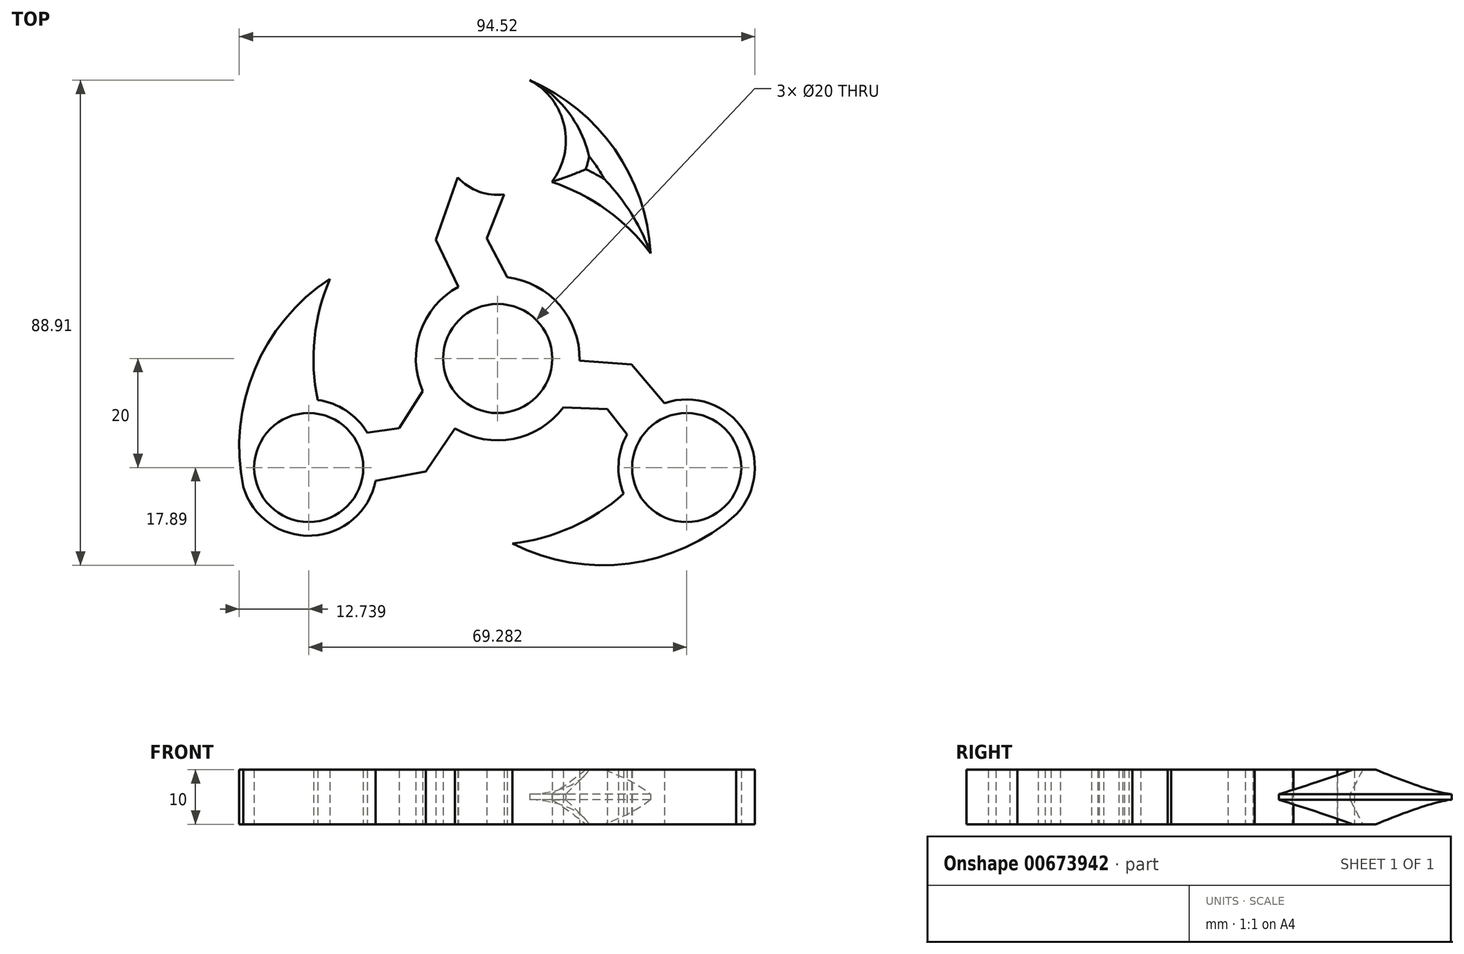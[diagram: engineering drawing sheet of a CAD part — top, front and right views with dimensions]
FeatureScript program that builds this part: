
annotation { "Feature Type Name" : "Feature", "Feature Type Description" : "" }
export const myFeature = defineFeature(function(context is Context, id is Id, definition is map)
    precondition{}
    {
        {
            var Q0;
            Q0=qCreatedBy(makeId("Top.planeOp"),FACE);
            var sketch = newSketch(context, id + "F0", { "sketchPlane" : qUnion([Q0])});
            skArc(sketch, "E0", {"start": v(-9.92, 38.75) * mm, "mid": v(0, -40) * mm, "end": v(9.92, 38.75) * mm});
            skCircle(sketch, "E1", {"center": v(0, 0) * mm, "radius": 10 * mm});
            skLineSegment(sketch, "E2", {"start": v(-5, 8.66) * mm, "end": v(-11.35, 21.78) * mm});
            skLineSegment(sketch, "E3", {"start": v(-11.35, 21.78) * mm, "end": v(-7.3, 33.18) * mm});
            skLineSegment(sketch, "E4", {"start": v(5, 8.66) * mm, "end": v(-2.01, 22.03) * mm});
            skLineSegment(sketch, "E5", {"start": v(-2.01, 22.03) * mm, "end": v(1.18, 30.07) * mm});
            skCircle(sketch, "E6", {"center": v(0, 40) * mm, "radius": 10 * mm});
            skCircle(sketch, "E7", {"center": v(0, 40) * mm, "radius": 12.5 * mm});
            skPoint(sketch, "E8.orphan", {"position": v(-5, 39.69) * mm});
            skPoint(sketch, "E9.orphan", {"position": v(5, 39.69) * mm});
            skCircle(sketch, "E10.1.0", {"center": v(-34.64, -20) * mm, "radius": 12.5 * mm});
            skCircle(sketch, "E10.1.1", {"center": v(-34.64, -20) * mm, "radius": 10 * mm});
            skLineSegment(sketch, "E10.1.2", {"start": v(-13.19, -20.72) * mm, "end": v(-25.08, -22.92) * mm});
            skLineSegment(sketch, "E10.1.3", {"start": v(-18.07, -12.76) * mm, "end": v(-26.63, -14.01) * mm});
            skLineSegment(sketch, "E10.1.4", {"start": v(-5, -8.66) * mm, "end": v(-13.19, -20.72) * mm});
            skLineSegment(sketch, "E10.1.5", {"start": v(-10, 0) * mm, "end": v(-18.07, -12.76) * mm});
            skCircle(sketch, "E10.2.0", {"center": v(34.64, -20) * mm, "radius": 12.5 * mm});
            skCircle(sketch, "E10.2.1", {"center": v(34.64, -20) * mm, "radius": 10 * mm});
            skLineSegment(sketch, "E10.2.2", {"start": v(24.54, -1.06) * mm, "end": v(32.39, -10.26) * mm});
            skLineSegment(sketch, "E10.2.3", {"start": v(20.08, -9.27) * mm, "end": v(25.45, -16.06) * mm});
            skLineSegment(sketch, "E10.2.4", {"start": v(10, 0) * mm, "end": v(24.54, -1.06) * mm});
            skLineSegment(sketch, "E10.2.5", {"start": v(5, -8.66) * mm, "end": v(20.08, -9.27) * mm});
            skCircle(sketch, "E11", {"center": v(0, 0) * mm, "radius": 15 * mm});
            skArc(sketch, "E12", {"start": v(28.04, 19.33) * mm, "mid": v(20.53, 39.6) * mm, "end": v(2.93, 52.15) * mm});
            skArc(sketch, "E13", {"start": v(28.04, 19.33) * mm, "mid": v(19.97, 27.24) * mm, "end": v(9.92, 32.4) * mm});
            skArc(sketch, "E14.1.0", {"start": v(-30.76, 14.62) * mm, "mid": v(-44.57, -2.02) * mm, "end": v(-46.63, -23.54) * mm});
            skArc(sketch, "E14.1.1", {"start": v(-30.76, 14.62) * mm, "mid": v(-33.58, 3.68) * mm, "end": v(-33.02, -7.6) * mm});
            skArc(sketch, "E14.2.0", {"start": v(2.72, -33.94) * mm, "mid": v(24.03, -37.59) * mm, "end": v(43.7, -28.61) * mm});
            skArc(sketch, "E14.2.1", {"start": v(2.72, -33.94) * mm, "mid": v(13.6, -30.92) * mm, "end": v(23.1, -24.8) * mm});
            skSolve(sketch);
        }
        {
            var Q0;
            {var subQ0=sQuery(id+"F0.wireOp",EDGE,"E6");var subQ1=sQuery(id+"F0.wireOp",EDGE,"E0");var subQ2=makeQuery(id+"F0.imprint","INTERSECT",VERTEX,{"disambiguationData":[OD(1.0)],"derivedFrom":[subQ1,subQ0]});Q0=makeQuery(id+"F0.imprint","IMPRINT",FACE,{"disambiguationData":[TD([[makeQuery(id+"F0.imprint","IMPRINT",EDGE,{"disambiguationData":[TD([[subQ2,1.0]])],"derivedFrom":subQ1}),1.0]])]});}
            var Q1;
            {var subQ0=sQuery(id+"F0.wireOp",EDGE,"E6");var subQ1=sQuery(id+"F0.wireOp",EDGE,"E0");var subQ2=makeQuery(id+"F0.imprint","INTERSECT",VERTEX,{"disambiguationData":[OD(0.0)],"derivedFrom":[subQ1,subQ0]});Q1=makeQuery(id+"F0.imprint","IMPRINT",FACE,{"disambiguationData":[TD([[makeQuery(id+"F0.imprint","IMPRINT",EDGE,{"disambiguationData":[TD([[subQ2,-1.0]])],"derivedFrom":subQ1}),-1.0]])]});}
            var Q2;
            {var subQ0=sQuery(id+"F0.wireOp",EDGE,"E6");var subQ1=sQuery(id+"F0.wireOp",EDGE,"E0");var subQ2=makeQuery(id+"F0.imprint","INTERSECT",VERTEX,{"disambiguationData":[OD(0.0)],"derivedFrom":[subQ1,subQ0]});Q2=makeQuery(id+"F0.imprint","IMPRINT",FACE,{"disambiguationData":[TD([[makeQuery(id+"F0.imprint","IMPRINT",EDGE,{"disambiguationData":[TD([[subQ2,-1.0]])],"derivedFrom":subQ1}),1.0]])]});}
            var Q3;
            {var subQ0=sQuery(id+"F0.wireOp",EDGE,"E6");var subQ1=sQuery(id+"F0.wireOp",EDGE,"E3");var subQ2=makeQuery(id+"F0.imprint","INTERSECT",VERTEX,{"derivedFrom":[subQ1,subQ0]});Q3=makeQuery(id+"F0.imprint","IMPRINT",FACE,{"disambiguationData":[TD([[makeQuery(id+"F0.imprint","IMPRINT",EDGE,{"disambiguationData":[TD([[subQ2,1.0]])],"derivedFrom":subQ1}),-1.0]])]});}
            var Q4;
            {var subQ5=sQuery(id+"F0.wireOp",EDGE,"E3");var subQ6=sQuery(id+"F0.wireOp",EDGE,"E2");var subQ7=makeQuery(id+"F0.imprint","INTERSECT",VERTEX,{"derivedFrom":[subQ6,subQ5]});Q4=makeQuery(id+"F0.imprint","IMPRINT",FACE,{"disambiguationData":[TD([[makeQuery(id+"F0.imprint","IMPRINT",EDGE,{"disambiguationData":[TD([[subQ7,1.0]])],"derivedFrom":subQ6}),-1.0]])]});}
            var Q5;
            {var subQ0=sQuery(id+"F0.wireOp",EDGE,"E2");var subQ1=sQuery(id+"F0.wireOp",EDGE,"E1");var subQ2=makeQuery(id+"F0.imprint","INTERSECT",VERTEX,{"derivedFrom":[subQ1,subQ0]});Q5=makeQuery(id+"F0.imprint","IMPRINT",FACE,{"disambiguationData":[TD([[makeQuery(id+"F0.imprint","IMPRINT",EDGE,{"disambiguationData":[TD([[subQ2,1.0]])],"derivedFrom":subQ1}),-1.0]])]});}
            var Q6;
            {var subQ0=sQuery(id+"F0.wireOp",EDGE,"E2");var subQ1=sQuery(id+"F0.wireOp",EDGE,"E1");var subQ2=makeQuery(id+"F0.imprint","INTERSECT",VERTEX,{"derivedFrom":[subQ1,subQ0]});Q6=makeQuery(id+"F0.imprint","IMPRINT",FACE,{"disambiguationData":[TD([[makeQuery(id+"F0.imprint","IMPRINT",EDGE,{"disambiguationData":[TD([[subQ2,-1.0]])],"derivedFrom":subQ1}),-1.0]])]});}
            var Q7;
            {var subQ0=sQuery(id+"F0.wireOp",EDGE,"E4");var subQ1=sQuery(id+"F0.wireOp",EDGE,"E1");var subQ2=makeQuery(id+"F0.imprint","INTERSECT",VERTEX,{"derivedFrom":[subQ1,subQ0]});Q7=makeQuery(id+"F0.imprint","IMPRINT",FACE,{"disambiguationData":[TD([[makeQuery(id+"F0.imprint","IMPRINT",EDGE,{"disambiguationData":[TD([[subQ2,1.0]])],"derivedFrom":subQ1}),-1.0]])]});}
            var Q8;
            {var subQ0=sQuery(id+"F0.wireOp",EDGE,"E10.2.4");var subQ1=sQuery(id+"F0.wireOp",EDGE,"E1");var subQ2=makeQuery(id+"F0.imprint","INTERSECT",VERTEX,{"derivedFrom":[subQ1,subQ0]});Q8=makeQuery(id+"F0.imprint","IMPRINT",FACE,{"disambiguationData":[TD([[makeQuery(id+"F0.imprint","IMPRINT",EDGE,{"disambiguationData":[TD([[subQ2,1.0]])],"derivedFrom":subQ1}),-1.0]])]});}
            var Q9;
            {var subQ0=sQuery(id+"F0.wireOp",EDGE,"E10.1.4");var subQ1=sQuery(id+"F0.wireOp",EDGE,"E1");var subQ2=makeQuery(id+"F0.imprint","INTERSECT",VERTEX,{"derivedFrom":[subQ1,subQ0]});Q9=makeQuery(id+"F0.imprint","IMPRINT",FACE,{"disambiguationData":[TD([[makeQuery(id+"F0.imprint","IMPRINT",EDGE,{"disambiguationData":[TD([[subQ2,-1.0]])],"derivedFrom":subQ1}),-1.0]])]});}
            var Q10;
            {var subQ0=sQuery(id+"F0.wireOp",EDGE,"E10.1.4");var subQ1=sQuery(id+"F0.wireOp",EDGE,"E1");var subQ2=makeQuery(id+"F0.imprint","INTERSECT",VERTEX,{"derivedFrom":[subQ1,subQ0]});Q10=makeQuery(id+"F0.imprint","IMPRINT",FACE,{"disambiguationData":[TD([[makeQuery(id+"F0.imprint","IMPRINT",EDGE,{"disambiguationData":[TD([[subQ2,1.0]])],"derivedFrom":subQ1}),-1.0]])]});}
            var Q11;
            {var subQ3=sQuery(id+"F0.wireOp",EDGE,"E10.1.0");var subQ6=sQuery(id+"F0.wireOp",EDGE,"E10.1.2");var subQ10=makeQuery(id+"F0.imprint","INTERSECT",VERTEX,{"derivedFrom":[subQ3,subQ6]});Q11=makeQuery(id+"F0.imprint","IMPRINT",FACE,{"disambiguationData":[TD([[makeQuery(id+"F0.imprint","IMPRINT",EDGE,{"disambiguationData":[TD([[subQ10,-1.0]])],"derivedFrom":subQ3}),-1.0]])]});}
            var Q12;
            {var subQ0=sQuery(id+"F0.wireOp",EDGE,"E10.1.2");var subQ1=sQuery(id+"F0.wireOp",EDGE,"E10.1.0");var subQ2=makeQuery(id+"F0.imprint","INTERSECT",VERTEX,{"derivedFrom":[subQ1,subQ0]});Q12=makeQuery(id+"F0.imprint","IMPRINT",FACE,{"disambiguationData":[TD([[makeQuery(id+"F0.imprint","IMPRINT",EDGE,{"disambiguationData":[TD([[subQ2,-1.0]])],"derivedFrom":subQ1}),1.0]])]});}
            var Q13;
            {var subQ0=sQuery(id+"F0.wireOp",EDGE,"E10.1.0");var subQ1=sQuery(id+"F0.wireOp",EDGE,"E0");var subQ2=makeQuery(id+"F0.imprint","INTERSECT",VERTEX,{"disambiguationData":[OD(0.0)],"derivedFrom":[subQ1,subQ0]});Q13=makeQuery(id+"F0.imprint","IMPRINT",FACE,{"disambiguationData":[TD([[makeQuery(id+"F0.imprint","IMPRINT",EDGE,{"disambiguationData":[TD([[subQ2,-1.0]])],"derivedFrom":subQ1}),-1.0]])]});}
            var Q14;
            {var subQ0=sQuery(id+"F0.wireOp",EDGE,"E10.1.0");var subQ1=sQuery(id+"F0.wireOp",EDGE,"E0");var subQ2=makeQuery(id+"F0.imprint","INTERSECT",VERTEX,{"disambiguationData":[OD(1.0)],"derivedFrom":[subQ1,subQ0]});Q14=makeQuery(id+"F0.imprint","IMPRINT",FACE,{"disambiguationData":[TD([[makeQuery(id+"F0.imprint","IMPRINT",EDGE,{"disambiguationData":[TD([[subQ2,1.0]])],"derivedFrom":subQ1}),1.0]])]});}
            var Q15;
            {var subQ3=sQuery(id+"F0.wireOp",EDGE,"E10.2.0");var subQ6=sQuery(id+"F0.wireOp",EDGE,"E10.2.2");var subQ10=makeQuery(id+"F0.imprint","INTERSECT",VERTEX,{"derivedFrom":[subQ3,subQ6]});Q15=makeQuery(id+"F0.imprint","IMPRINT",FACE,{"disambiguationData":[TD([[makeQuery(id+"F0.imprint","IMPRINT",EDGE,{"disambiguationData":[TD([[subQ10,-1.0]])],"derivedFrom":subQ3}),-1.0]])]});}
            var Q16;
            {var subQ0=sQuery(id+"F0.wireOp",EDGE,"E10.2.2");var subQ1=sQuery(id+"F0.wireOp",EDGE,"E10.2.0");var subQ2=makeQuery(id+"F0.imprint","INTERSECT",VERTEX,{"derivedFrom":[subQ1,subQ0]});Q16=makeQuery(id+"F0.imprint","IMPRINT",FACE,{"disambiguationData":[TD([[makeQuery(id+"F0.imprint","IMPRINT",EDGE,{"disambiguationData":[TD([[subQ2,-1.0]])],"derivedFrom":subQ1}),1.0]])]});}
            var Q17;
            {var subQ0=sQuery(id+"F0.wireOp",EDGE,"E10.2.0");var subQ1=sQuery(id+"F0.wireOp",EDGE,"E0");var subQ2=makeQuery(id+"F0.imprint","INTERSECT",VERTEX,{"disambiguationData":[OD(1.0)],"derivedFrom":[subQ1,subQ0]});Q17=makeQuery(id+"F0.imprint","IMPRINT",FACE,{"disambiguationData":[TD([[makeQuery(id+"F0.imprint","IMPRINT",EDGE,{"disambiguationData":[TD([[subQ2,1.0]])],"derivedFrom":subQ1}),1.0]])]});}
            var Q18;
            {var subQ0=sQuery(id+"F0.wireOp",EDGE,"E10.2.0");var subQ1=sQuery(id+"F0.wireOp",EDGE,"E0");var subQ2=makeQuery(id+"F0.imprint","INTERSECT",VERTEX,{"disambiguationData":[OD(0.0)],"derivedFrom":[subQ1,subQ0]});Q18=makeQuery(id+"F0.imprint","IMPRINT",FACE,{"disambiguationData":[TD([[makeQuery(id+"F0.imprint","IMPRINT",EDGE,{"disambiguationData":[TD([[subQ2,-1.0]])],"derivedFrom":subQ1}),-1.0]])]});}
            var Q19;
            {var subQ0=sQuery(id+"F0.wireOp",EDGE,"E12");var subQ1=sQuery(id+"F0.wireOp",EDGE,"E0");var subQ2=makeQuery(id+"F0.imprint","INTERSECT",VERTEX,{"derivedFrom":[subQ1,subQ0]});Q19=makeQuery(id+"F0.imprint","IMPRINT",FACE,{"disambiguationData":[TD([[makeQuery(id+"F0.imprint","IMPRINT",EDGE,{"disambiguationData":[TD([[subQ2,-1.0]])],"derivedFrom":subQ1}),-1.0]])]});}
            var Q20;
            {var subQ5=sQuery(id+"F0.wireOp",EDGE,"E13");Q20=makeQuery(id+"F0.imprint","IMPRINT",FACE,{"disambiguationData":[TD([[makeQuery(id+"F0.imprint","IMPRINT",EDGE,{"derivedFrom":subQ5}),-1.0]])]});}
            var Q21;
            {var subQ0=sQuery(id+"F0.wireOp",EDGE,"E14.2.0");var subQ1=sQuery(id+"F0.wireOp",EDGE,"E0");var subQ2=makeQuery(id+"F0.imprint","INTERSECT",VERTEX,{"derivedFrom":[subQ1,subQ0]});Q21=makeQuery(id+"F0.imprint","IMPRINT",FACE,{"disambiguationData":[TD([[makeQuery(id+"F0.imprint","IMPRINT",EDGE,{"disambiguationData":[TD([[subQ2,-1.0]])],"derivedFrom":subQ1}),-1.0]])]});}
            var Q22;
            {var subQ3=sQuery(id+"F0.wireOp",EDGE,"E0");var subQ5=sQuery(id+"F0.wireOp",EDGE,"E10.2.0");var subQ8=makeQuery(id+"F0.imprint","INTERSECT",VERTEX,{"disambiguationData":[OD(1.0)],"derivedFrom":[subQ3,subQ5]});Q22=makeQuery(id+"F0.imprint","IMPRINT",FACE,{"disambiguationData":[TD([[makeQuery(id+"F0.imprint","IMPRINT",EDGE,{"disambiguationData":[TD([[subQ8,-1.0]])],"derivedFrom":subQ3}),1.0]])]});}
            var Q23;
            {var subQ1=sQuery(id+"F0.wireOp",EDGE,"E10.2.0");var subQ3=sQuery(id+"F0.wireOp",EDGE,"E0");var subQ4=makeQuery(id+"F0.imprint","INTERSECT",VERTEX,{"disambiguationData":[OD(1.0)],"derivedFrom":[subQ3,subQ1]});Q23=makeQuery(id+"F0.imprint","IMPRINT",FACE,{"disambiguationData":[TD([[makeQuery(id+"F0.imprint","IMPRINT",EDGE,{"disambiguationData":[TD([[subQ4,-1.0]])],"derivedFrom":subQ3}),-1.0]])]});}
            var Q24;
            {var subQ0=sQuery(id+"F0.wireOp",EDGE,"E10.2.0");var subQ1=sQuery(id+"F0.wireOp",EDGE,"E0");var subQ2=makeQuery(id+"F0.imprint","INTERSECT",VERTEX,{"disambiguationData":[OD(0.0)],"derivedFrom":[subQ1,subQ0]});Q24=makeQuery(id+"F0.imprint","IMPRINT",FACE,{"disambiguationData":[TD([[makeQuery(id+"F0.imprint","IMPRINT",EDGE,{"disambiguationData":[TD([[subQ2,1.0]])],"derivedFrom":subQ1}),1.0]])]});}
            var Q25;
            {var subQ0=sQuery(id+"F0.wireOp",EDGE,"E10.1.0");var subQ1=sQuery(id+"F0.wireOp",EDGE,"E0");var subQ2=makeQuery(id+"F0.imprint","INTERSECT",VERTEX,{"disambiguationData":[OD(0.0)],"derivedFrom":[subQ1,subQ0]});Q25=makeQuery(id+"F0.imprint","IMPRINT",FACE,{"disambiguationData":[TD([[makeQuery(id+"F0.imprint","IMPRINT",EDGE,{"disambiguationData":[TD([[subQ2,1.0]])],"derivedFrom":subQ1}),1.0]])]});}
            var Q26;
            {var subQ0=sQuery(id+"F0.wireOp",EDGE,"E10.1.0");var subQ2=sQuery(id+"F0.wireOp",EDGE,"E0");var subQ3=makeQuery(id+"F0.imprint","INTERSECT",VERTEX,{"disambiguationData":[OD(1.0)],"derivedFrom":[subQ2,subQ0]});Q26=makeQuery(id+"F0.imprint","IMPRINT",FACE,{"disambiguationData":[TD([[makeQuery(id+"F0.imprint","IMPRINT",EDGE,{"disambiguationData":[TD([[subQ3,-1.0]])],"derivedFrom":subQ2}),1.0]])]});}
            var Q27;
            {var subQ1=sQuery(id+"F0.wireOp",EDGE,"E10.1.0");var subQ3=sQuery(id+"F0.wireOp",EDGE,"E0");var subQ4=makeQuery(id+"F0.imprint","INTERSECT",VERTEX,{"disambiguationData":[OD(1.0)],"derivedFrom":[subQ3,subQ1]});Q27=makeQuery(id+"F0.imprint","IMPRINT",FACE,{"disambiguationData":[TD([[makeQuery(id+"F0.imprint","IMPRINT",EDGE,{"disambiguationData":[TD([[subQ4,-1.0]])],"derivedFrom":subQ3}),-1.0]])]});}
            var Q28;
            {var subQ0=sQuery(id+"F0.wireOp",EDGE,"E14.1.0");var subQ1=sQuery(id+"F0.wireOp",EDGE,"E0");var subQ2=makeQuery(id+"F0.imprint","INTERSECT",VERTEX,{"derivedFrom":[subQ1,subQ0]});Q28=makeQuery(id+"F0.imprint","IMPRINT",FACE,{"disambiguationData":[TD([[makeQuery(id+"F0.imprint","IMPRINT",EDGE,{"disambiguationData":[TD([[subQ2,-1.0]])],"derivedFrom":subQ1}),-1.0]])]});}
            extrude(context, id + "F1", {"entities" : qUnion([Q0, Q1, Q2, Q3, Q4, Q5, Q6, Q7, Q8, Q9, Q10, Q11, Q12, Q13, Q14, Q15, Q16, Q17, Q18, Q19, Q20, Q21, Q22, Q23, Q24, Q25, Q26, Q27, Q28]), "depth" : 10 * mm, "offsetDistance" : 25 * mm});
        }
        {
            var Q0;
            {var subQ0=sQuery(id+"F0.wireOp",EDGE,"E10.2.0");Q0=makeQuery(id+"F1.opExtrude","CAP_EDGE",EDGE,{"disambiguationData":[OSD([subQ0]),TDD([makeQuery(id+"F0.imprint","IMPRINT",EDGE,{"disambiguationData":[TD([[makeQuery(id+"F0.imprint","INTERSECT",VERTEX,{"derivedFrom":[subQ0,sQuery(id+"F0.wireOp",EDGE,"E14.2.1")]}),1.0]])],"derivedFrom":subQ0})])],"isStart":true});}
            var Q1;
            {var subQ0=sQuery(id+"F0.wireOp",EDGE,"E10.1.0");var subQ1=makeQuery(id+"F0.imprint","INTERSECT",VERTEX,{"disambiguationData":[OD(0.0)],"derivedFrom":[sQuery(id+"F0.wireOp",EDGE,"E0"),subQ0]});Q1=makeQuery(id+"F1.opExtrude","CAP_EDGE",EDGE,{"disambiguationData":[OSD([subQ0]),TDD([makeQuery(id+"F0.imprint","IMPRINT",EDGE,{"disambiguationData":[TD([[makeQuery(id+"F0.imprint","INTERSECT",VERTEX,{"disambiguationData":[OD(0.0)],"derivedFrom":[subQ0,sQuery(id+"F0.wireOp",EDGE,"E14.1.0")]}),-1.0]])],"derivedFrom":subQ0}),makeQuery(id+"F0.imprint","IMPRINT",EDGE,{"disambiguationData":[TD([[subQ1,-1.0]])],"derivedFrom":subQ0})])],"isStart":false});}
            var Q2;
            {var subQ0=sQuery(id+"F0.wireOp",EDGE,"E10.1.0");Q2=makeQuery(id+"F1.opExtrude","CAP_EDGE",EDGE,{"disambiguationData":[OSD([subQ0]),TDD([makeQuery(id+"F0.imprint","IMPRINT",EDGE,{"disambiguationData":[TD([[makeQuery(id+"F0.imprint","INTERSECT",VERTEX,{"derivedFrom":[subQ0,sQuery(id+"F0.wireOp",EDGE,"E14.1.1")]}),1.0]])],"derivedFrom":subQ0})])],"isStart":false});}
            var Q3;
            Q3=makeQuery(id+"F1.opExtrude","CAP_EDGE",EDGE,{"disambiguationData":[OSD([sQuery(id+"F0.wireOp",EDGE,"E10.1.2")])],"isStart":false});
            var Q4;
            Q4=makeQuery(id+"F1.opExtrude","CAP_EDGE",EDGE,{"disambiguationData":[OSD([sQuery(id+"F0.wireOp",EDGE,"E10.1.4")])],"isStart":false});
            var Q5;
            {var subQ0=sQuery(id+"F0.wireOp",EDGE,"E11");Q5=makeQuery(id+"F1.opExtrude","CAP_EDGE",EDGE,{"disambiguationData":[OSD([subQ0]),TDD([makeQuery(id+"F0.imprint","IMPRINT",EDGE,{"disambiguationData":[TD([[makeQuery(id+"F0.imprint","INTERSECT",VERTEX,{"derivedFrom":[sQuery(id+"F0.wireOp",EDGE,"E10.1.4"),subQ0]}),-1.0]])],"derivedFrom":subQ0})])],"isStart":false});}
            var Q6;
            Q6=makeQuery(id+"F1.opExtrude","CAP_EDGE",EDGE,{"disambiguationData":[OSD([sQuery(id+"F0.wireOp",EDGE,"E10.2.5")])],"isStart":false});
            var Q7;
            Q7=makeQuery(id+"F1.opExtrude","CAP_EDGE",EDGE,{"disambiguationData":[OSD([sQuery(id+"F0.wireOp",EDGE,"E10.2.3")])],"isStart":false});
            var Q8;
            {var subQ0=sQuery(id+"F0.wireOp",EDGE,"E10.2.0");var subQ1=makeQuery(id+"F0.imprint","INTERSECT",VERTEX,{"disambiguationData":[OD(0.0)],"derivedFrom":[sQuery(id+"F0.wireOp",EDGE,"E0"),subQ0]});Q8=makeQuery(id+"F1.opExtrude","CAP_EDGE",EDGE,{"disambiguationData":[OSD([subQ0]),TDD([makeQuery(id+"F0.imprint","IMPRINT",EDGE,{"disambiguationData":[TD([[makeQuery(id+"F0.imprint","INTERSECT",VERTEX,{"disambiguationData":[OD(0.0)],"derivedFrom":[subQ0,sQuery(id+"F0.wireOp",EDGE,"E14.2.0")]}),-1.0]])],"derivedFrom":subQ0}),makeQuery(id+"F0.imprint","IMPRINT",EDGE,{"disambiguationData":[TD([[subQ1,-1.0]])],"derivedFrom":subQ0})])],"isStart":false});}
            var Q9;
            {var subQ0=sQuery(id+"F0.wireOp",EDGE,"E10.2.0");Q9=makeQuery(id+"F1.opExtrude","CAP_EDGE",EDGE,{"disambiguationData":[OSD([subQ0]),TDD([makeQuery(id+"F0.imprint","IMPRINT",EDGE,{"disambiguationData":[TD([[makeQuery(id+"F0.imprint","INTERSECT",VERTEX,{"derivedFrom":[subQ0,sQuery(id+"F0.wireOp",EDGE,"E14.2.1")]}),1.0]])],"derivedFrom":subQ0})])],"isStart":false});}
            var Q10;
            Q10=makeQuery(id+"F1.opExtrude","CAP_EDGE",EDGE,{"disambiguationData":[OSD([sQuery(id+"F0.wireOp",EDGE,"E10.1.5")])],"isStart":false});
            var Q11;
            Q11=makeQuery(id+"F1.opExtrude","CAP_EDGE",EDGE,{"disambiguationData":[OSD([sQuery(id+"F0.wireOp",EDGE,"E10.1.3")])],"isStart":false});
            var Q12;
            Q12=makeQuery(id+"F1.opExtrude","CAP_EDGE",EDGE,{"disambiguationData":[OSD([sQuery(id+"F0.wireOp",EDGE,"E10.2.2")])],"isStart":false});
            var Q13;
            Q13=makeQuery(id+"F1.opExtrude","CAP_EDGE",EDGE,{"disambiguationData":[OSD([sQuery(id+"F0.wireOp",EDGE,"E10.2.4")])],"isStart":false});
            var Q14;
            {var subQ0=sQuery(id+"F0.wireOp",EDGE,"E11");Q14=makeQuery(id+"F1.opExtrude","CAP_EDGE",EDGE,{"disambiguationData":[OSD([subQ0]),TDD([makeQuery(id+"F0.imprint","IMPRINT",EDGE,{"disambiguationData":[TD([[makeQuery(id+"F0.imprint","INTERSECT",VERTEX,{"derivedFrom":[sQuery(id+"F0.wireOp",EDGE,"E4"),subQ0]}),1.0]])],"derivedFrom":subQ0})])],"isStart":false});}
            var Q15;
            Q15=makeQuery(id+"F1.opExtrude","CAP_EDGE",EDGE,{"disambiguationData":[OSD([sQuery(id+"F0.wireOp",EDGE,"E4")])],"isStart":false});
            var Q16;
            Q16=makeQuery(id+"F1.opExtrude","CAP_EDGE",EDGE,{"disambiguationData":[OSD([sQuery(id+"F0.wireOp",EDGE,"E5")])],"isStart":false});
            var Q17;
            {var subQ0=sQuery(id+"F0.wireOp",EDGE,"E7");var subQ1=makeQuery(id+"F0.imprint","INTERSECT",VERTEX,{"disambiguationData":[OD(0.0)],"derivedFrom":[sQuery(id+"F0.wireOp",EDGE,"E0"),subQ0]});Q17=makeQuery(id+"F1.opExtrude","CAP_EDGE",EDGE,{"disambiguationData":[OSD([subQ0]),TDD([makeQuery(id+"F0.imprint","IMPRINT",EDGE,{"disambiguationData":[TD([[makeQuery(id+"F0.imprint","INTERSECT",VERTEX,{"disambiguationData":[OD(0.0)],"derivedFrom":[subQ0,sQuery(id+"F0.wireOp",EDGE,"E12")]}),-1.0]])],"derivedFrom":subQ0}),makeQuery(id+"F0.imprint","IMPRINT",EDGE,{"disambiguationData":[TD([[subQ1,-1.0]])],"derivedFrom":subQ0})])],"isStart":false});}
            var Q18;
            {var subQ0=sQuery(id+"F0.wireOp",EDGE,"E7");Q18=makeQuery(id+"F1.opExtrude","CAP_EDGE",EDGE,{"disambiguationData":[OSD([subQ0]),TDD([makeQuery(id+"F0.imprint","IMPRINT",EDGE,{"disambiguationData":[TD([[makeQuery(id+"F0.imprint","INTERSECT",VERTEX,{"derivedFrom":[subQ0,sQuery(id+"F0.wireOp",EDGE,"E13")]}),1.0]])],"derivedFrom":subQ0})])],"isStart":false});}
            var Q19;
            Q19=makeQuery(id+"F1.opExtrude","CAP_EDGE",EDGE,{"disambiguationData":[OSD([sQuery(id+"F0.wireOp",EDGE,"E3")])],"isStart":false});
            var Q20;
            Q20=makeQuery(id+"F1.opExtrude","CAP_EDGE",EDGE,{"disambiguationData":[OSD([sQuery(id+"F0.wireOp",EDGE,"E2")])],"isStart":false});
            var Q21;
            {var subQ0=sQuery(id+"F0.wireOp",EDGE,"E11");Q21=makeQuery(id+"F1.opExtrude","CAP_EDGE",EDGE,{"disambiguationData":[OSD([subQ0]),TDD([makeQuery(id+"F0.imprint","IMPRINT",EDGE,{"disambiguationData":[TD([[makeQuery(id+"F0.imprint","INTERSECT",VERTEX,{"derivedFrom":[sQuery(id+"F0.wireOp",EDGE,"E2"),subQ0]}),-1.0]])],"derivedFrom":subQ0})])],"isStart":false});}
            var Q22;
            {var subQ0=sQuery(id+"F0.wireOp",EDGE,"E7");var subQ1=makeQuery(id+"F0.imprint","INTERSECT",VERTEX,{"disambiguationData":[OD(0.0)],"derivedFrom":[sQuery(id+"F0.wireOp",EDGE,"E0"),subQ0]});Q22=makeQuery(id+"F1.opExtrude","CAP_EDGE",EDGE,{"disambiguationData":[OSD([subQ0]),TDD([makeQuery(id+"F0.imprint","IMPRINT",EDGE,{"disambiguationData":[TD([[makeQuery(id+"F0.imprint","INTERSECT",VERTEX,{"disambiguationData":[OD(0.0)],"derivedFrom":[subQ0,sQuery(id+"F0.wireOp",EDGE,"E12")]}),-1.0]])],"derivedFrom":subQ0}),makeQuery(id+"F0.imprint","IMPRINT",EDGE,{"disambiguationData":[TD([[subQ1,-1.0]])],"derivedFrom":subQ0})])],"isStart":true});}
            var Q23;
            {var subQ0=sQuery(id+"F0.wireOp",EDGE,"E7");Q23=makeQuery(id+"F1.opExtrude","CAP_EDGE",EDGE,{"disambiguationData":[OSD([subQ0]),TDD([makeQuery(id+"F0.imprint","IMPRINT",EDGE,{"disambiguationData":[TD([[makeQuery(id+"F0.imprint","INTERSECT",VERTEX,{"derivedFrom":[subQ0,sQuery(id+"F0.wireOp",EDGE,"E13")]}),1.0]])],"derivedFrom":subQ0})])],"isStart":true});}
            var Q24;
            Q24=makeQuery(id+"F1.opExtrude","CAP_EDGE",EDGE,{"disambiguationData":[OSD([sQuery(id+"F0.wireOp",EDGE,"E3")])],"isStart":true});
            var Q25;
            Q25=makeQuery(id+"F1.opExtrude","CAP_EDGE",EDGE,{"disambiguationData":[OSD([sQuery(id+"F0.wireOp",EDGE,"E2")])],"isStart":true});
            var Q26;
            {var subQ0=sQuery(id+"F0.wireOp",EDGE,"E11");Q26=makeQuery(id+"F1.opExtrude","CAP_EDGE",EDGE,{"disambiguationData":[OSD([subQ0]),TDD([makeQuery(id+"F0.imprint","IMPRINT",EDGE,{"disambiguationData":[TD([[makeQuery(id+"F0.imprint","INTERSECT",VERTEX,{"derivedFrom":[sQuery(id+"F0.wireOp",EDGE,"E2"),subQ0]}),-1.0]])],"derivedFrom":subQ0})])],"isStart":true});}
            var Q27;
            Q27=makeQuery(id+"F1.opExtrude","CAP_EDGE",EDGE,{"disambiguationData":[OSD([sQuery(id+"F0.wireOp",EDGE,"E10.1.5")])],"isStart":true});
            var Q28;
            Q28=makeQuery(id+"F1.opExtrude","CAP_EDGE",EDGE,{"disambiguationData":[OSD([sQuery(id+"F0.wireOp",EDGE,"E10.1.3")])],"isStart":true});
            var Q29;
            {var subQ0=sQuery(id+"F0.wireOp",EDGE,"E10.1.0");var subQ1=makeQuery(id+"F0.imprint","INTERSECT",VERTEX,{"disambiguationData":[OD(0.0)],"derivedFrom":[sQuery(id+"F0.wireOp",EDGE,"E0"),subQ0]});Q29=makeQuery(id+"F1.opExtrude","CAP_EDGE",EDGE,{"disambiguationData":[OSD([subQ0]),TDD([makeQuery(id+"F0.imprint","IMPRINT",EDGE,{"disambiguationData":[TD([[makeQuery(id+"F0.imprint","INTERSECT",VERTEX,{"disambiguationData":[OD(0.0)],"derivedFrom":[subQ0,sQuery(id+"F0.wireOp",EDGE,"E14.1.0")]}),-1.0]])],"derivedFrom":subQ0}),makeQuery(id+"F0.imprint","IMPRINT",EDGE,{"disambiguationData":[TD([[subQ1,-1.0]])],"derivedFrom":subQ0})])],"isStart":true});}
            var Q30;
            {var subQ0=sQuery(id+"F0.wireOp",EDGE,"E10.1.0");Q30=makeQuery(id+"F1.opExtrude","CAP_EDGE",EDGE,{"disambiguationData":[OSD([subQ0]),TDD([makeQuery(id+"F0.imprint","IMPRINT",EDGE,{"disambiguationData":[TD([[makeQuery(id+"F0.imprint","INTERSECT",VERTEX,{"derivedFrom":[subQ0,sQuery(id+"F0.wireOp",EDGE,"E14.1.1")]}),1.0]])],"derivedFrom":subQ0})])],"isStart":true});}
            var Q31;
            Q31=makeQuery(id+"F1.opExtrude","CAP_EDGE",EDGE,{"disambiguationData":[OSD([sQuery(id+"F0.wireOp",EDGE,"E10.1.2")])],"isStart":true});
            var Q32;
            Q32=makeQuery(id+"F1.opExtrude","CAP_EDGE",EDGE,{"disambiguationData":[OSD([sQuery(id+"F0.wireOp",EDGE,"E10.1.4")])],"isStart":true});
            var Q33;
            {var subQ0=sQuery(id+"F0.wireOp",EDGE,"E11");Q33=makeQuery(id+"F1.opExtrude","CAP_EDGE",EDGE,{"disambiguationData":[OSD([subQ0]),TDD([makeQuery(id+"F0.imprint","IMPRINT",EDGE,{"disambiguationData":[TD([[makeQuery(id+"F0.imprint","INTERSECT",VERTEX,{"derivedFrom":[sQuery(id+"F0.wireOp",EDGE,"E10.1.4"),subQ0]}),-1.0]])],"derivedFrom":subQ0})])],"isStart":true});}
            var Q34;
            Q34=makeQuery(id+"F1.opExtrude","CAP_EDGE",EDGE,{"disambiguationData":[OSD([sQuery(id+"F0.wireOp",EDGE,"E10.2.5")])],"isStart":true});
            var Q35;
            Q35=makeQuery(id+"F1.opExtrude","CAP_EDGE",EDGE,{"disambiguationData":[OSD([sQuery(id+"F0.wireOp",EDGE,"E10.2.3")])],"isStart":true});
            var Q36;
            Q36=makeQuery(id+"F1.opExtrude","CAP_EDGE",EDGE,{"disambiguationData":[OSD([sQuery(id+"F0.wireOp",EDGE,"E10.2.2")])],"isStart":true});
            var Q37;
            Q37=makeQuery(id+"F1.opExtrude","CAP_EDGE",EDGE,{"disambiguationData":[OSD([sQuery(id+"F0.wireOp",EDGE,"E10.2.4")])],"isStart":true});
            var Q38;
            {var subQ0=sQuery(id+"F0.wireOp",EDGE,"E11");Q38=makeQuery(id+"F1.opExtrude","CAP_EDGE",EDGE,{"disambiguationData":[OSD([subQ0]),TDD([makeQuery(id+"F0.imprint","IMPRINT",EDGE,{"disambiguationData":[TD([[makeQuery(id+"F0.imprint","INTERSECT",VERTEX,{"derivedFrom":[sQuery(id+"F0.wireOp",EDGE,"E4"),subQ0]}),1.0]])],"derivedFrom":subQ0})])],"isStart":true});}
            var Q39;
            Q39=makeQuery(id+"F1.opExtrude","CAP_EDGE",EDGE,{"disambiguationData":[OSD([sQuery(id+"F0.wireOp",EDGE,"E5")])],"isStart":true});
            var Q40;
            Q40=makeQuery(id+"F1.opExtrude","CAP_EDGE",EDGE,{"disambiguationData":[OSD([sQuery(id+"F0.wireOp",EDGE,"E4")])],"isStart":true});
            var Q41;
            Q41=makeQuery(id+"F1.opExtrude","CAP_EDGE",EDGE,{"disambiguationData":[OSD([sQuery(id+"F0.wireOp",EDGE,"E14.1.0")])],"isStart":false});
            var Q42;
            Q42=makeQuery(id+"F1.opExtrude","CAP_EDGE",EDGE,{"disambiguationData":[OSD([sQuery(id+"F0.wireOp",EDGE,"E14.1.1")])],"isStart":false});
            var Q43;
            Q43=makeQuery(id+"F1.opExtrude","CAP_EDGE",EDGE,{"disambiguationData":[OSD([sQuery(id+"F0.wireOp",EDGE,"E14.2.0")])],"isStart":false});
            var Q44;
            Q44=makeQuery(id+"F1.opExtrude","CAP_EDGE",EDGE,{"disambiguationData":[OSD([sQuery(id+"F0.wireOp",EDGE,"E14.2.1")])],"isStart":false});
            var Q45;
            Q45=makeQuery(id+"F1.opExtrude","CAP_EDGE",EDGE,{"disambiguationData":[OSD([sQuery(id+"F0.wireOp",EDGE,"E13")])],"isStart":false});
            var Q46;
            Q46=makeQuery(id+"F1.opExtrude","CAP_EDGE",EDGE,{"disambiguationData":[OSD([sQuery(id+"F0.wireOp",EDGE,"E12")])],"isStart":false});
            var Q47;
            Q47=makeQuery(id+"F1.opExtrude","CAP_EDGE",EDGE,{"disambiguationData":[OSD([sQuery(id+"F0.wireOp",EDGE,"E12")])],"isStart":true});
            var Q48;
            Q48=makeQuery(id+"F1.opExtrude","CAP_EDGE",EDGE,{"disambiguationData":[OSD([sQuery(id+"F0.wireOp",EDGE,"E13")])],"isStart":true});
            var Q49;
            Q49=makeQuery(id+"F1.opExtrude","CAP_EDGE",EDGE,{"disambiguationData":[OSD([sQuery(id+"F0.wireOp",EDGE,"E14.2.1")])],"isStart":true});
            var Q50;
            Q50=makeQuery(id+"F1.opExtrude","CAP_EDGE",EDGE,{"disambiguationData":[OSD([sQuery(id+"F0.wireOp",EDGE,"E14.2.0")])],"isStart":true});
            var Q51;
            {var subQ0=sQuery(id+"F0.wireOp",EDGE,"E10.2.0");var subQ1=makeQuery(id+"F0.imprint","INTERSECT",VERTEX,{"disambiguationData":[OD(0.0)],"derivedFrom":[sQuery(id+"F0.wireOp",EDGE,"E0"),subQ0]});Q51=makeQuery(id+"F1.opExtrude","CAP_EDGE",EDGE,{"disambiguationData":[OSD([subQ0]),TDD([makeQuery(id+"F0.imprint","IMPRINT",EDGE,{"disambiguationData":[TD([[makeQuery(id+"F0.imprint","INTERSECT",VERTEX,{"disambiguationData":[OD(0.0)],"derivedFrom":[subQ0,sQuery(id+"F0.wireOp",EDGE,"E14.2.0")]}),-1.0]])],"derivedFrom":subQ0}),makeQuery(id+"F0.imprint","IMPRINT",EDGE,{"disambiguationData":[TD([[subQ1,-1.0]])],"derivedFrom":subQ0})])],"isStart":true});}
            var Q52;
            Q52=makeQuery(id+"F1.opExtrude","CAP_EDGE",EDGE,{"disambiguationData":[OSD([sQuery(id+"F0.wireOp",EDGE,"E14.1.1")])],"isStart":true});
            var Q53;
            Q53=makeQuery(id+"F1.opExtrude","CAP_EDGE",EDGE,{"disambiguationData":[OSD([sQuery(id+"F0.wireOp",EDGE,"E14.1.0")])],"isStart":true});
            chamfer(context, id + "F2", {"entities" : qUnion([Q0, Q1, Q2, Q3, Q4, Q5, Q6, Q7, Q8, Q9, Q10, Q11, Q12, Q13, Q14, Q15, Q16, Q17, Q18, Q19, Q20, Q21, Q22, Q23, Q24, Q25, Q26, Q27, Q28, Q29, Q30, Q31, Q32, Q33, Q34, Q35, Q36, Q37, Q38, Q39, Q40, Q41, Q42, Q43, Q44, Q45, Q46, Q47, Q48, Q49, Q50, Q51, Q52, Q53]), "width" : 4.5 * mm, "tangentPropagation" : true});
        }
    });
